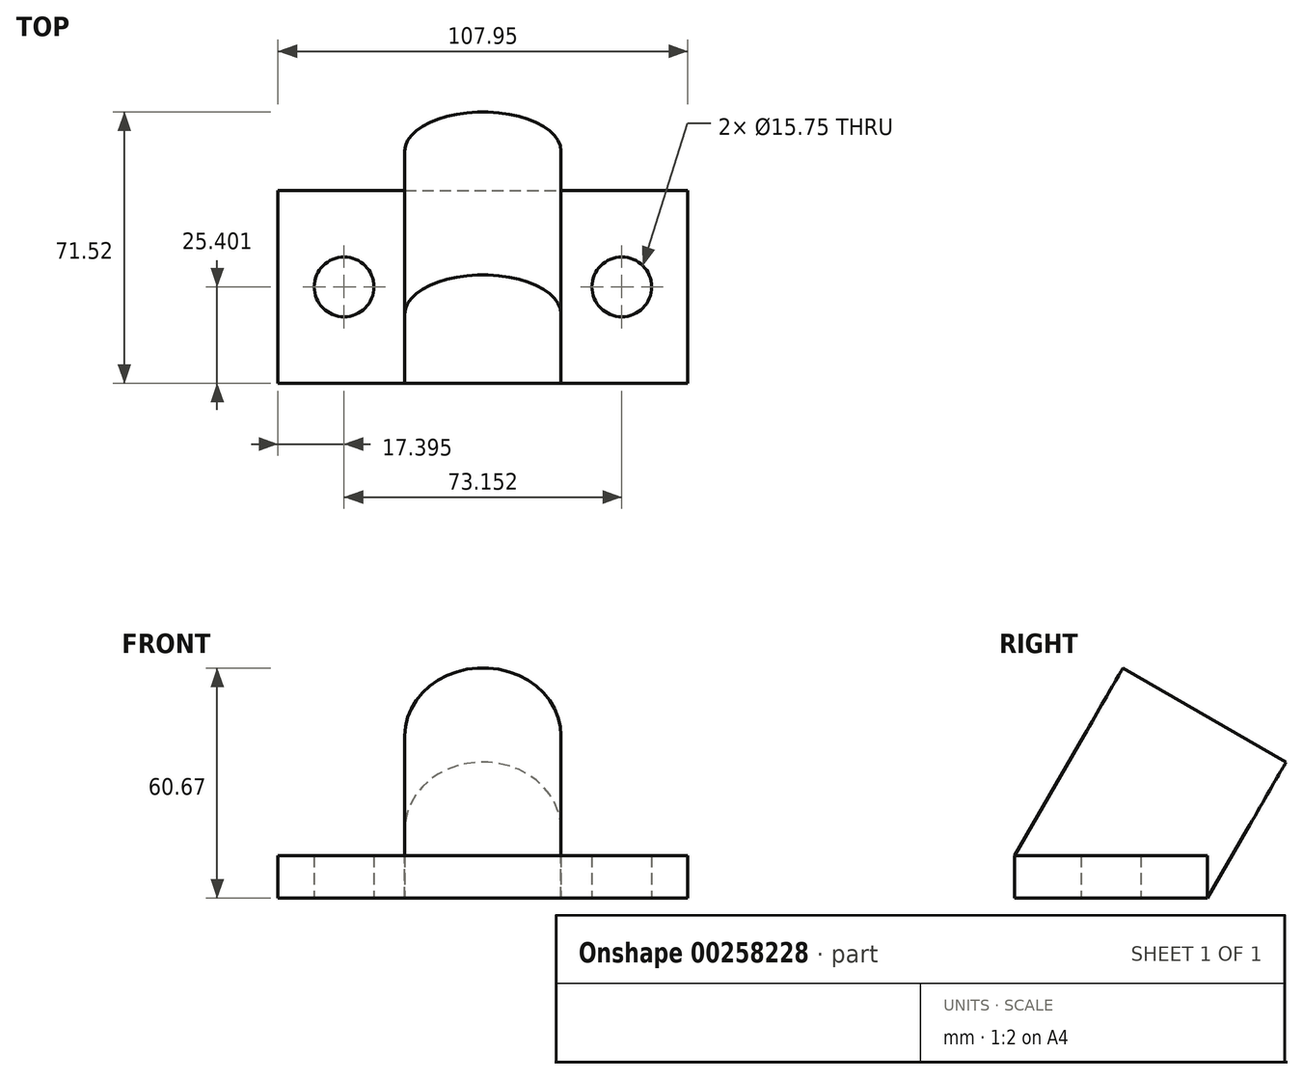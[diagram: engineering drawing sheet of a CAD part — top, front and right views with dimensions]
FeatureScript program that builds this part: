
annotation { "Feature Type Name" : "Feature", "Feature Type Description" : "" }
export const myFeature = defineFeature(function(context is Context, id is Id, definition is map)
    precondition{}
    {
        {
            var Q0;
            Q0=qCreatedBy(makeId("Top.planeOp"),FACE);
            var sketch = newSketch(context, id + "F0", { "sketchPlane" : qUnion([Q0])});
            skLineSegment(sketch, "E0.bottom", {"start": v(-35.7, 26.17) * mm, "end": v(72.25, 26.17) * mm});
            skLineSegment(sketch, "E0.top", {"start": v(-35.7, -24.63) * mm, "end": v(72.25, -24.63) * mm});
            skLineSegment(sketch, "E0.left", {"start": v(-35.7, 26.17) * mm, "end": v(-35.7, -24.63) * mm});
            skLineSegment(sketch, "E0.right", {"start": v(72.25, 26.17) * mm, "end": v(72.25, -24.63) * mm});
            skCircle(sketch, "E1", {"center": v(-18.3, 0.77) * mm, "radius": 7.87 * mm});
            skCircle(sketch, "E2", {"center": v(54.85, 0.77) * mm, "radius": 7.87 * mm});
            skLineSegment(sketch, "E3", {"start": v(-18.3, 0.77) * mm, "end": v(-35.7, 0.77) * mm, "construction": true});
            skLineSegment(sketch, "E4", {"start": v(-18.3, 0.77) * mm, "end": v(-18.3, -24.63) * mm, "construction": true});
            skLineSegment(sketch, "E5", {"start": v(54.85, 0.77) * mm, "end": v(72.25, 0.77) * mm, "construction": true});
            skLineSegment(sketch, "E6", {"start": v(54.85, 0.77) * mm, "end": v(54.85, -24.63) * mm, "construction": true});
            skSolve(sketch);
        }
        {
            var Q0;
            Q0=makeQuery(id+"F0.imprint","IMPRINT",FACE,{"disambiguationData":[TD([[makeQuery(id+"F0.imprint","IMPRINT",EDGE,{"derivedFrom":sQuery(id+"F0.wireOp",EDGE,"E0.bottom")}),-1.0]])]});
            extrude(context, id + "F1", {"entities" : qUnion([Q0]), "depth" : 11.18 * mm});
        }
        {
            var Q0;
            Q0=makeQuery(id+"F1.opExtrude","SWEPT_FACE",FACE,{"disambiguationData":[OSD([sQuery(id+"F0.wireOp",EDGE,"E0.left")])]});
            var sketch = newSketch(context, id + "F2", { "sketchPlane" : qUnion([Q0])});
            skLineSegment(sketch, "E7", {"start": v(24.63, 11.18) * mm, "end": v(6.34, 42.85) * mm});
            skLineSegment(sketch, "E8", {"start": v(-26.17, 0) * mm, "end": v(-36.6, 18.06) * mm});
            skLineSegment(sketch, "E9", {"start": v(6.34, 42.85) * mm, "end": v(-36.6, 18.06) * mm});
            skLineSegment(sketch, "E10", {"start": v(-36.6, 18.06) * mm, "end": v(-46.89, 35.88) * mm});
            skLineSegment(sketch, "E11", {"start": v(-46.89, 35.88) * mm, "end": v(-3.95, 60.67) * mm});
            skLineSegment(sketch, "E12", {"start": v(6.34, 42.85) * mm, "end": v(-3.95, 60.67) * mm});
            skLineSegment(sketch, "E13", {"start": v(24.63, 11.18) * mm, "end": v(-26.17, 11.18) * mm});
            skLineSegment(sketch, "E14", {"start": v(-26.17, 11.18) * mm, "end": v(-26.17, 0) * mm});
            skSolve(sketch);
        }
        {
            var Q0;
            Q0=makeQuery(id+"F2.imprint","IMPRINT",FACE,{"disambiguationData":[TD([[makeQuery(id+"F2.imprint","IMPRINT",EDGE,{"derivedFrom":sQuery(id+"F2.wireOp",EDGE,"E7")}),1.0]])]});
            var Q1;
            Q1=sQuery(id+"F2.wireOp",EDGE,"E7");
            var Q2;
            Q2=sQuery(id+"F2.wireOp",EDGE,"E9");
            var Q3;
            Q3=sQuery(id+"F2.wireOp",EDGE,"E8");
            var Q4;
            Q4=sQuery(id+"F2.wireOp",EDGE,"E13");
            var Q5;
            Q5=sQuery(id+"F2.wireOp",EDGE,"E14");
            extrude(context, id + "F3", {"entities" : qUnion([Q0]), "surfaceEntities" : qUnion([Q1, Q2, Q3, Q4, Q5]), "oppositeDirection" : true, "depth" : 33.4 * mm});
        }
        {
            var Q0;
            Q0=makeQuery(id+"F3.opExtrude","CAP_FACE",FACE,{"disambiguationData":[OSD([sQuery(id+"F2.wireOp",EDGE,"E7"),sQuery(id+"F2.wireOp",EDGE,"E8"),sQuery(id+"F2.wireOp",EDGE,"E9"),sQuery(id+"F2.wireOp",EDGE,"E13"),sQuery(id+"F2.wireOp",EDGE,"E14")])],"isStart":false});
            extrude(context, id + "F4", {"entities" : qUnion([Q0]), "operationType" : NewBodyOperationType.ADD, "depth" : 41.15 * mm});
        }
        {
            var Q0;
            Q0=makeQuery(id+"F2.imprint","IMPRINT",FACE,{"disambiguationData":[TD([[makeQuery(id+"F2.imprint","IMPRINT",EDGE,{"derivedFrom":sQuery(id+"F2.wireOp",EDGE,"E7")}),1.0]])]});
            extrude(context, id + "F5", {"entities" : qUnion([Q0]), "operationType" : NewBodyOperationType.REMOVE, "oppositeDirection" : true, "depth" : 33.4 * mm});
        }
        {
            var Q0;
            {var subQ0=sQuery(id+"F2.wireOp",EDGE,"E7");Q0=makeQuery(id+"F4.boolean.opBoolean","MERGE",FACE,{"derivedFrom":[makeQuery(id+"F3.opExtrude","SWEPT_FACE",FACE,{"disambiguationData":[OSD([subQ0])]}),makeQuery(id+"F4.opExtrude","SWEPT_FACE",FACE,{"disambiguationData":[OSD([subQ0])]})]});}
            var sketch = newSketch(context, id + "F6", { "sketchPlane" : qUnion([Q0])});
            skLineSegment(sketch, "E15.bottom", {"start": v(-2.3, 33.94) * mm, "end": v(38.84, 33.94) * mm});
            skLineSegment(sketch, "E15.top", {"start": v(-2.3, 54.51) * mm, "end": v(38.84, 54.51) * mm});
            skLineSegment(sketch, "E15.left", {"start": v(-2.3, 33.94) * mm, "end": v(-2.3, 54.51) * mm});
            skLineSegment(sketch, "E15.right", {"start": v(38.84, 33.94) * mm, "end": v(38.84, 54.51) * mm});
            skSolve(sketch);
        }
        {
            var Q0;
            Q0=makeQuery(id+"F6.imprint","IMPRINT",FACE,{"disambiguationData":[TD([[makeQuery(id+"F6.imprint","IMPRINT",EDGE,{"derivedFrom":sQuery(id+"F6.wireOp",EDGE,"E15.bottom")}),-1.0]])]});
            var Q1;
            {var subQ0=sQuery(id+"F2.wireOp",EDGE,"E8");Q1=makeQuery(id+"F4.boolean.opBoolean","MERGE",FACE,{"derivedFrom":[makeQuery(id+"F3.opExtrude","SWEPT_FACE",FACE,{"disambiguationData":[OSD([subQ0])]}),makeQuery(id+"F4.opExtrude","SWEPT_FACE",FACE,{"disambiguationData":[OSD([subQ0])]})]});}
            extrude(context, id + "F7", {"entities" : qUnion([Q0]), "operationType" : NewBodyOperationType.ADD, "endBound" : BoundingType.UP_TO_SURFACE, "oppositeDirection" : true, "endBoundEntityFace" : qUnion([Q1]), "depth" : 25.4 * mm});
        }
        {
            var Q0;
            Q0=makeQuery(id+"F7.opExtrude","SWEPT_EDGE",EDGE,{"disambiguationData":[OSD([sQuery(id+"F6.wireOp",EDGE,"E15.top"),sQuery(id+"F6.wireOp",EDGE,"E15.right")])]});
            var Q1;
            Q1=makeQuery(id+"F7.opExtrude","SWEPT_EDGE",EDGE,{"disambiguationData":[OSD([sQuery(id+"F6.wireOp",EDGE,"E15.top"),sQuery(id+"F6.wireOp",EDGE,"E15.left")])]});
            fillet(context, id + "F8", {"entities" : qUnion([Q0, Q1]), "radius" : 20.57 * mm, "tangentPropagation" : true, "allowEdgeOverflow" : false});
        }
    });
